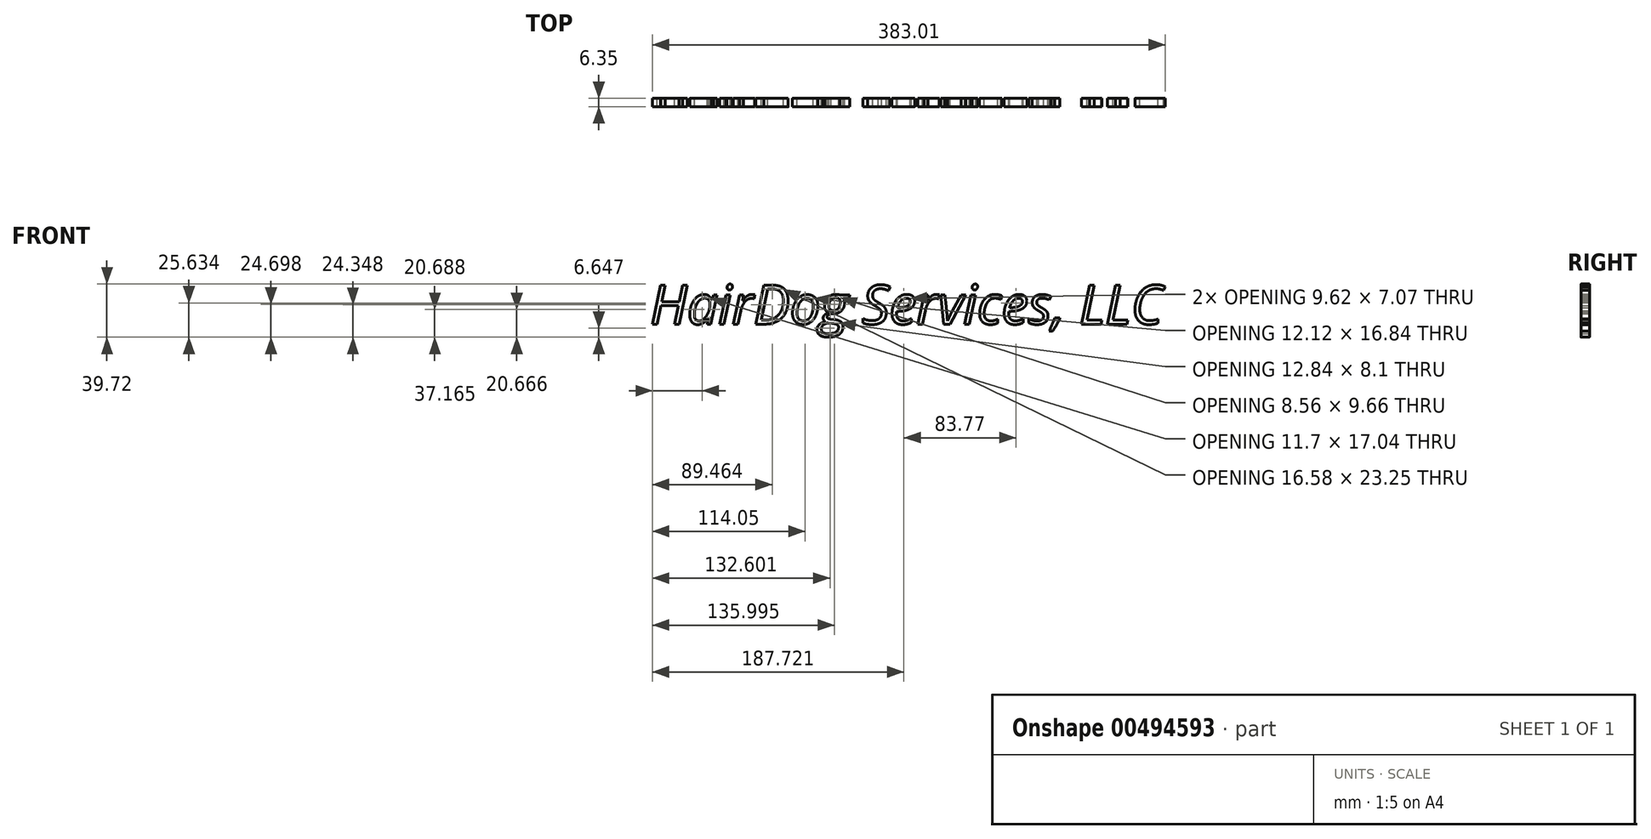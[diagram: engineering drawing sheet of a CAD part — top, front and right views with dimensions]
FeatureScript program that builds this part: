
annotation { "Feature Type Name" : "Feature", "Feature Type Description" : "" }
export const myFeature = defineFeature(function(context is Context, id is Id, definition is map)
    precondition{}
    {
        {
            var Q0;
            Q0=qCreatedBy(makeId("Front.planeOp"),FACE);
            var sketch = newSketch(context, id + "F0", { "sketchPlane" : qUnion([Q0])});
            skText(sketch, "E0", { "text": "HairDog Services, LLC", "fontName": "OpenSans-Italic.ttf"});
            const initialGuessF0  = {"E0": [-0.05916, 0.01249, 1, 0, 0.02935]};
            skSetInitialGuess(sketch, initialGuessF0);
            skSolve(sketch);
        }
        {
            var Q0;
            Q0 = qSketchRegion(id + "F0", true);
            extrude(context, id + "F1", {"entities" : qUnion([Q0]), "depth" : 6.35 * mm});
        }
    });
